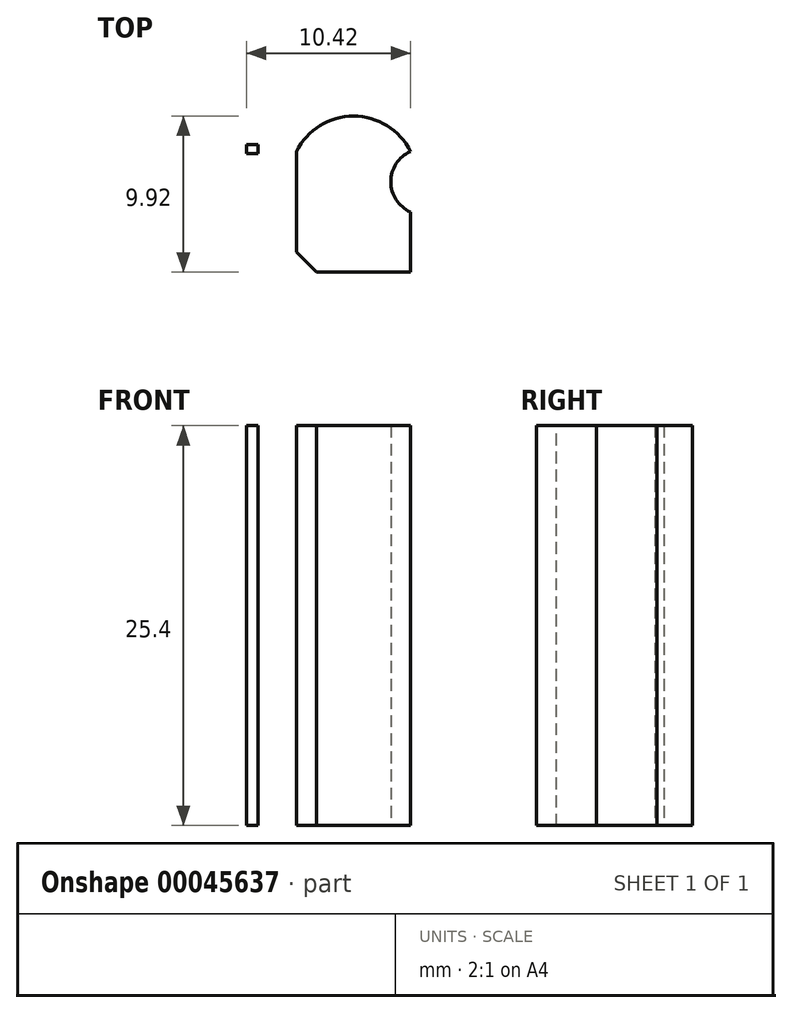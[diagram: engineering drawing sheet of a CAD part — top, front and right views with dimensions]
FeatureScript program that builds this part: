
annotation { "Feature Type Name" : "Feature", "Feature Type Description" : "" }
export const myFeature = defineFeature(function(context is Context, id is Id, definition is map)
    precondition{}
    {
        {
            var Q0;
            Q0=qCreatedBy(makeId("Top.planeOp"),FACE);
            var sketch = newSketch(context, id + "F0", { "sketchPlane" : qUnion([Q0])});
            skLineSegment(sketch, "E0.bottom", {"start": v(-10.87, 10.5) * mm, "end": v(-10.14, 10.5) * mm});
            skLineSegment(sketch, "E0.top", {"start": v(-10.87, 9.94) * mm, "end": v(-10.14, 9.94) * mm});
            skLineSegment(sketch, "E0.left", {"start": v(-10.87, 10.5) * mm, "end": v(-10.87, 9.94) * mm});
            skLineSegment(sketch, "E0.right", {"start": v(-10.14, 10.5) * mm, "end": v(-10.14, 9.94) * mm});
            skLineSegment(sketch, "E1.bottom", {"start": v(-7.69, 10.07) * mm, "end": v(-0.45, 10.07) * mm});
            skLineSegment(sketch, "E1.top", {"start": v(-7.69, 2.4) * mm, "end": v(-0.45, 2.4) * mm});
            skLineSegment(sketch, "E1.left", {"start": v(-7.69, 10.07) * mm, "end": v(-7.69, 2.4) * mm});
            skArc(sketch, "E2", {"start": v(-0.45, 10.07) * mm, "mid": v(-4.07, 12.33) * mm, "end": v(-7.69, 10.07) * mm});
            skLineSegment(sketch, "E3", {"start": v(-7.69, 4.95) * mm, "end": v(-3, 4.95) * mm});
            skLineSegment(sketch, "E4", {"start": v(-3, 4.95) * mm, "end": v(-3, 2.4) * mm});
            skLineSegment(sketch, "E5", {"start": v(-0.45, 2.4) * mm, "end": v(-0.45, 6.24) * mm});
            skArc(sketch, "E6", {"start": v(-0.45, 10.07) * mm, "mid": v(-1.7, 8.15) * mm, "end": v(-0.45, 6.24) * mm});
            skLineSegment(sketch, "E7", {"start": v(-0.45, 6.24) * mm, "end": v(-0.45, 2.4) * mm});
            skSolve(sketch);
        }
        {
            var Q0;
            Q0 = qSketchRegion(id + "F0", true);
            var Q1;
            {var subQ1=sQuery(id+"F0.wireOp",EDGE,"E1.bottom");Q1=makeQuery(id+"F0.imprint","IMPRINT",FACE,{"disambiguationData":[TD([[makeQuery(id+"F0.imprint","IMPRINT",EDGE,{"derivedFrom":subQ1}),-1.0]])]});}
            extrude(context, id + "F1", {"entities" : qUnion([Q0, Q1]), "depth" : 25.4 * mm});
        }
        {
            var Q0;
            Q0=makeQuery(id+"F1.opExtrude","SWEPT_EDGE",EDGE,{"disambiguationData":[OSD([sQuery(id+"F0.wireOp",EDGE,"E1.top"),sQuery(id+"F0.wireOp",EDGE,"E1.left")])]});
            chamfer(context, id + "F2", {"entities" : qUnion([Q0]), "width" : 1.27 * mm, "tangentPropagation" : true});
        }
    });
